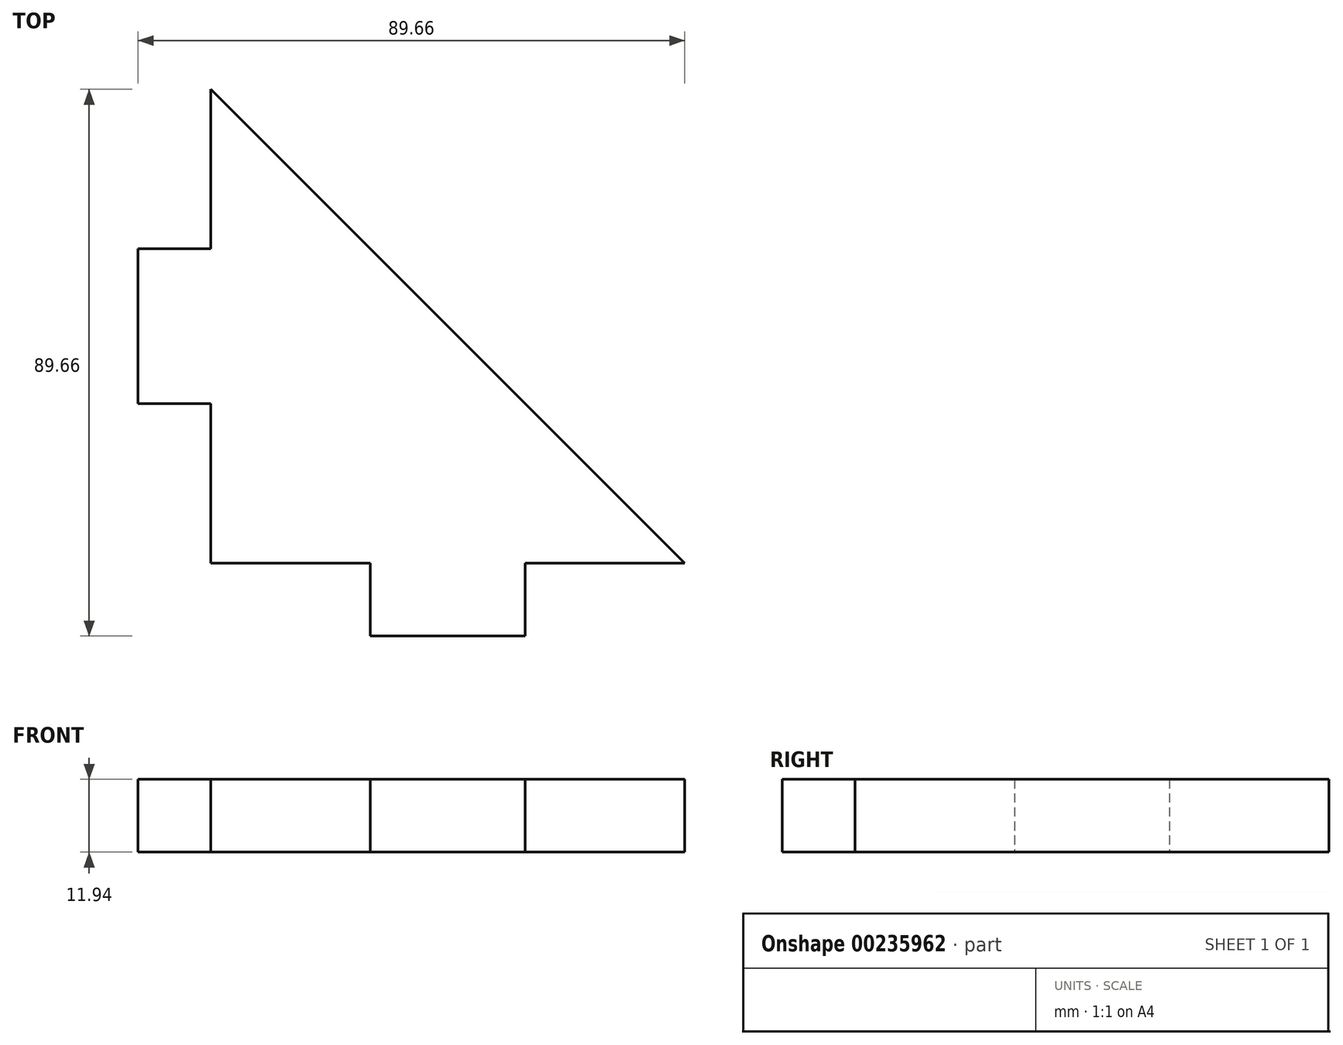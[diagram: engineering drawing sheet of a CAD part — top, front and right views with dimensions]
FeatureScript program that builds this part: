
annotation { "Feature Type Name" : "Feature", "Feature Type Description" : "" }
export const myFeature = defineFeature(function(context is Context, id is Id, definition is map)
    precondition{}
    {
        {
            var Q0;
            Q0=qCreatedBy(makeId("Top.planeOp"),FACE);
            var sketch = newSketch(context, id + "F0", { "sketchPlane" : qUnion([Q0])});
            skLineSegment(sketch, "E0", {"start": v(0, 0) * mm, "end": v(0, 77.72) * mm});
            skLineSegment(sketch, "E1", {"start": v(0, 0) * mm, "end": v(77.72, 0) * mm});
            skLineSegment(sketch, "E2", {"start": v(0, 77.72) * mm, "end": v(77.72, 0) * mm});
            skLineSegment(sketch, "E3", {"start": v(26.16, 0) * mm, "end": v(26.16, -11.94) * mm});
            skLineSegment(sketch, "E4", {"start": v(51.56, 0) * mm, "end": v(51.56, -11.94) * mm});
            skLineSegment(sketch, "E5", {"start": v(26.16, -11.94) * mm, "end": v(51.56, -11.94) * mm});
            skLineSegment(sketch, "E6", {"start": v(0, 51.56) * mm, "end": v(-11.94, 51.56) * mm});
            skLineSegment(sketch, "E7", {"start": v(0, 26.16) * mm, "end": v(-11.94, 26.16) * mm});
            skLineSegment(sketch, "E8", {"start": v(-11.94, 51.56) * mm, "end": v(-11.94, 26.16) * mm});
            skSolve(sketch);
        }
        {
            var Q0;
            {var subQ4=sQuery(id+"F0.wireOp",EDGE,"E2");Q0=makeQuery(id+"F0.imprint","IMPRINT",FACE,{"disambiguationData":[TD([[makeQuery(id+"F0.imprint","IMPRINT",EDGE,{"derivedFrom":subQ4}),-1.0]])]});}
            extrude(context, id + "F1", {"entities" : qUnion([Q0]), "depth" : 11.94 * mm});
        }
        {
            var Q0;
            {var subQ0=sQuery(id+"F0.wireOp",EDGE,"E6");Q0=makeQuery(id+"F0.imprint","IMPRINT",FACE,{"disambiguationData":[TD([[makeQuery(id+"F0.imprint","IMPRINT",EDGE,{"derivedFrom":subQ0}),1.0]])]});}
            var Q1;
            {var subQ0=sQuery(id+"F0.wireOp",EDGE,"E3");Q1=makeQuery(id+"F0.imprint","IMPRINT",FACE,{"disambiguationData":[TD([[makeQuery(id+"F0.imprint","IMPRINT",EDGE,{"derivedFrom":subQ0}),1.0]])]});}
            extrude(context, id + "F2", {"entities" : qUnion([Q0, Q1]), "operationType" : NewBodyOperationType.ADD, "depth" : 11.94 * mm});
        }
    });
